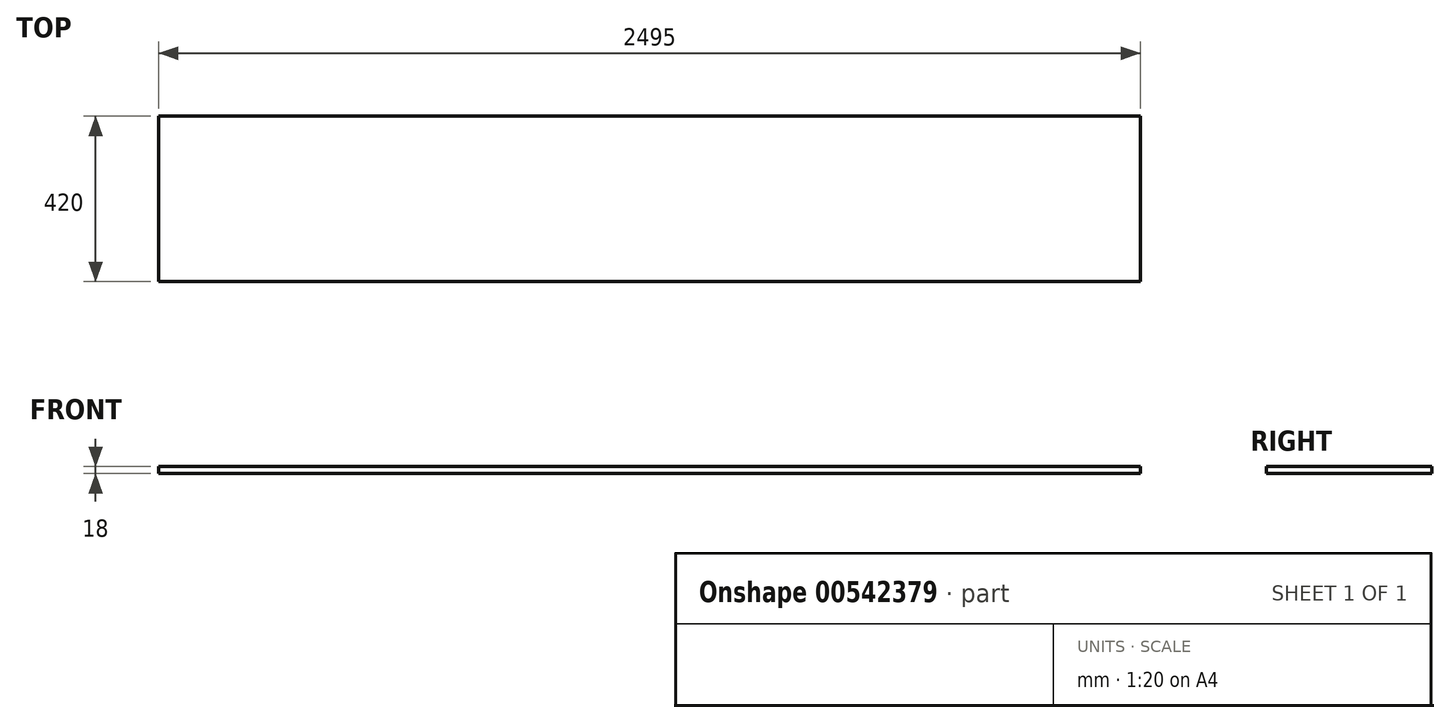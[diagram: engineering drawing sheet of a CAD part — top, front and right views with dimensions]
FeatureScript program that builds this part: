
annotation { "Feature Type Name" : "Feature", "Feature Type Description" : "" }
export const myFeature = defineFeature(function(context is Context, id is Id, definition is map)
    precondition{}
    {
        {
            var Q0;
            Q0=qCreatedBy(makeId("Front.planeOp"),FACE);
            var sketch = newSketch(context, id + "F0", { "sketchPlane" : qUnion([Q0])});
            skLineSegment(sketch, "E0.bottom", {"start": v(-1182.88, -130.92) * mm, "end": v(1312.12, -130.92) * mm});
            skLineSegment(sketch, "E0.top", {"start": v(-1182.88, -112.92) * mm, "end": v(1312.12, -112.92) * mm});
            skLineSegment(sketch, "E0.left", {"start": v(-1182.88, -130.92) * mm, "end": v(-1182.88, -112.92) * mm});
            skLineSegment(sketch, "E0.right", {"start": v(1312.12, -130.92) * mm, "end": v(1312.12, -112.92) * mm});
            skSolve(sketch);
        }
        {
            var Q0;
            Q0 = qSketchRegion(id + "F0", true);
            extrude(context, id + "F1", {"entities" : qUnion([Q0]), "oppositeDirection" : true, "depth" : 420 * mm, "offsetDistance" : 25 * mm});
        }
    });
